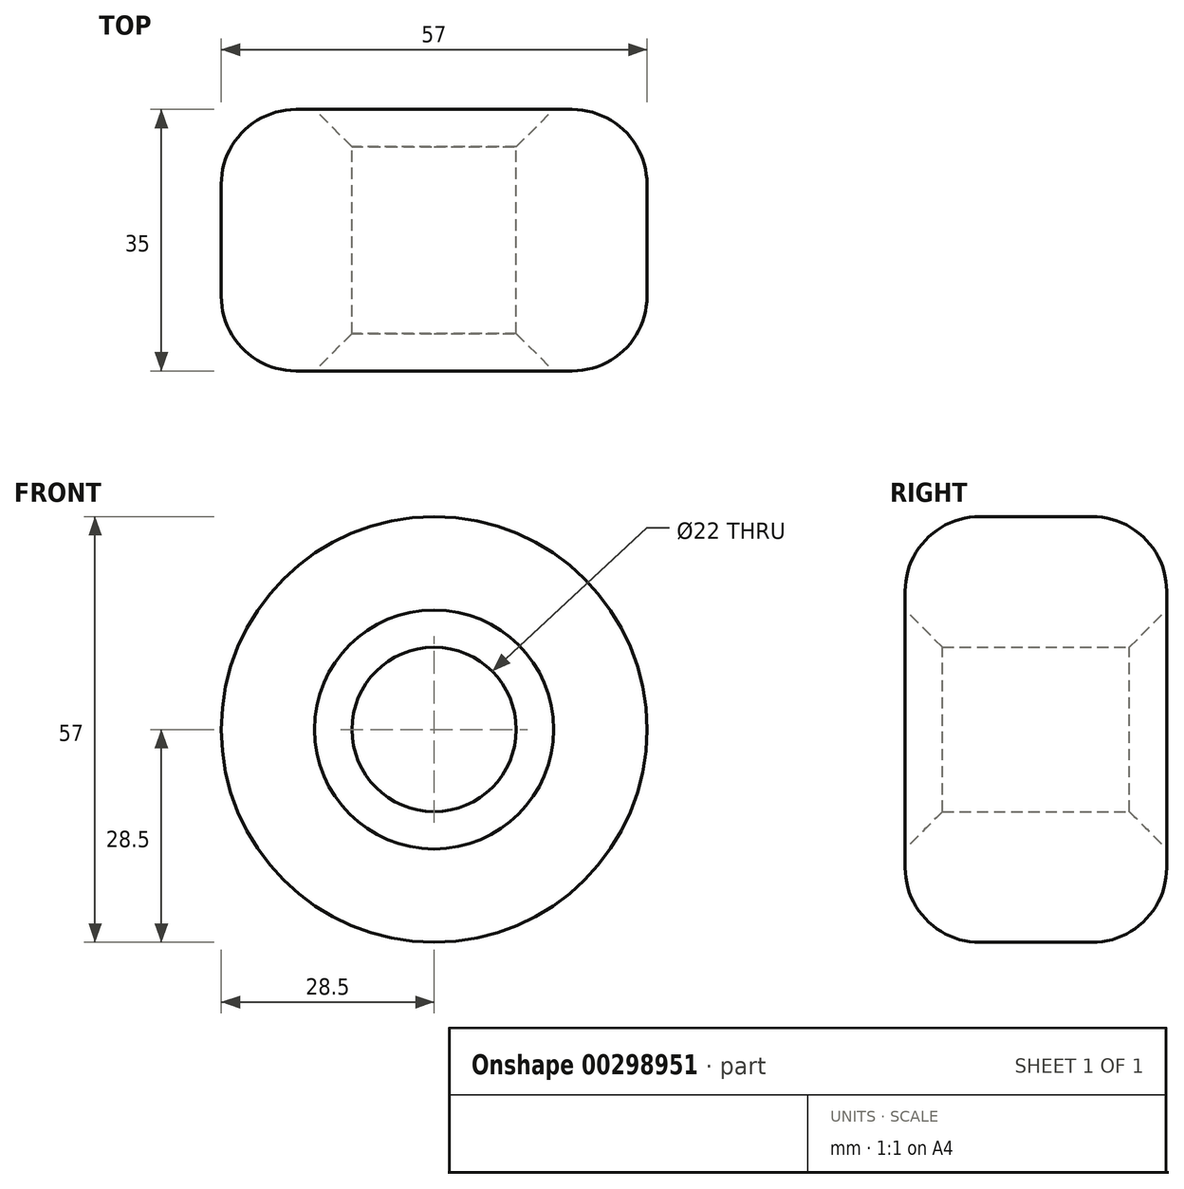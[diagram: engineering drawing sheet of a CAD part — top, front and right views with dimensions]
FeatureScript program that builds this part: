
annotation { "Feature Type Name" : "Feature", "Feature Type Description" : "" }
export const myFeature = defineFeature(function(context is Context, id is Id, definition is map)
    precondition{}
    {
        {
            var Q0;
            Q0=qCreatedBy(makeId("Front.planeOp"),FACE);
            var sketch = newSketch(context, id + "F0", { "sketchPlane" : qUnion([Q0])});
            skCircle(sketch, "E0", {"center": v(0, 0) * mm, "radius": 28.5 * mm});
            skCircle(sketch, "E1", {"center": v(0, 0) * mm, "radius": 11 * mm});
            skSolve(sketch);
        }
        {
            var Q0;
            Q0 = qSketchRegion(id + "F0", true);
            extrude(context, id + "F1", {"entities" : qUnion([Q0]), "endBound" : BoundingType.SYMMETRIC, "depth" : 35 * mm});
        }
        {
            var Q0;
            Q0=makeQuery(id+"F1.opExtrude","CAP_EDGE",EDGE,{"disambiguationData":[OSD([sQuery(id+"F0.wireOp",EDGE,"E0")])],"isStart":false});
            var Q1;
            Q1=makeQuery(id+"F1.opExtrude","CAP_EDGE",EDGE,{"disambiguationData":[OSD([sQuery(id+"F0.wireOp",EDGE,"E0")])],"isStart":true});
            fillet(context, id + "F2", {"entities" : qUnion([Q0, Q1]), "radius" : 10 * mm, "tangentPropagation" : true, "allowEdgeOverflow" : false});
        }
        {
            var Q0;
            Q0=makeQuery(id+"F1.opExtrude","SWEPT_FACE",FACE,{"disambiguationData":[OSD([sQuery(id+"F0.wireOp",EDGE,"E0")])]});
            var Q1;
            Q1=makeQuery(id+"F1.opExtrude","CAP_EDGE",EDGE,{"disambiguationData":[OSD([sQuery(id+"F0.wireOp",EDGE,"E1")])],"isStart":false});
            var Q2;
            Q2=makeQuery(id+"F1.opExtrude","CAP_EDGE",EDGE,{"disambiguationData":[OSD([sQuery(id+"F0.wireOp",EDGE,"E1")])],"isStart":true});
            chamfer(context, id + "F3", {"entities" : qUnion([Q0, Q1, Q2]), "width" : 5 * mm, "tangentPropagation" : true});
        }
    });
